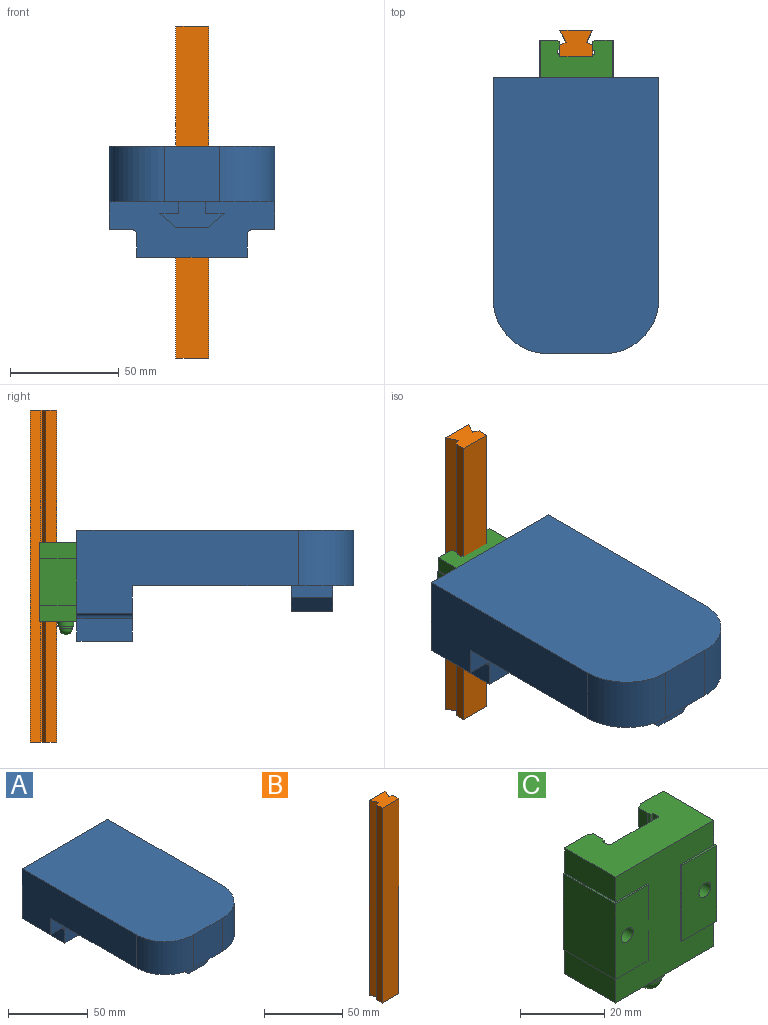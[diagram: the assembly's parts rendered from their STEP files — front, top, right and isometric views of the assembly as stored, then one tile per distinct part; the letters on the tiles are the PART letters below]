
ASSEMBLY  parts=3 mates=4
PART A: 25 faces, bbox 76.2x127x50.8 mm
  f0: plane 76.2x25.4mm, normal (0,-1,0), area 1615.7mm2, adj f1,f2,f3,f4,f5,f7,f8,f9
  f1: plane 50.8x25.4mm, normal (0,0,-1), area 1290.3mm2, adj f0,f2,f10,f11
  f2: plane 25.4x10.16mm, normal (1,0,0), area 258.1mm2, adj f0,f1,f3,f11
  f3: cylinder r=2.54mm len=25.4mm, axis (0,-1,0), area 101.3mm2, adj f0,f2,f4,f11
  f4: plane 25.4x10.16mm, normal (0,0,-1), area 258.1mm2, adj f0,f3,f5,f11
  f5: plane 101.6x38.1mm, normal (1,0,0), area 2903.2mm2, adj f0,f4,f6,f11,f13,f15
  f6: plane 127x76.2mm, normal (0,0,1), area 9400.5mm2, adj f5,f7,f11,f12,f14,f15
  f7: plane 101.6x38.1mm, normal (-1,0,0), area 2903.2mm2, adj f0,f6,f8,f11,f13,f14
  f8: plane 25.4x10.16mm, normal (0,0,-1), area 258.1mm2, adj f0,f7,f9,f11
  f9: cylinder r=2.54mm len=25.4mm, axis (0,-1,0), area 101.3mm2, adj f0,f8,f10,f11
  f10: plane 25.4x10.16mm, normal (-1,0,0), area 258.1mm2, adj f0,f1,f9,f11
  f11: plane 76.2x50.8mm, normal (0,1,0), area 3551.1mm2, adj f1,f2,f3,f4,f5,f6,f7,f8
  f12: plane 25.4x25.4mm, normal (0,-1,0), area 645.2mm2, adj f6,f13,f14,f15
  f13: plane 101.6x76.2mm, normal (0,0,-1), area 7223.1mm2, adj f0,f5,f7,f12,f14,f15,f16,f22
  f14: cylinder r=25.4mm len=25.4mm, axis (0,0,1), area 1013.4mm2, adj f6,f7,f12,f13
  f15: cylinder r=25.4mm len=25.4mm, axis (0,0,-1), area 1013.4mm2, adj f5,f6,f12,f13
  f16: plane 19.05x5.44mm, normal (-1,0,0), area 103.6mm2, adj f13,f17,f23,f24
  f17: plane 19.05x8.37mm, normal (0,0,1), area 159.4mm2, adj f16,f18,f23,f24
  f18: plane 19.05x7.1mm, normal (-0.67,0,-0.75), area 181.4mm2, adj f17,f19,f23,f24
  f19: plane 19.05x15.24mm, normal (0,0,-1), area 290.3mm2, adj f18,f20,f23,f24
  f20: plane 19.05x7.1mm, normal (0.67,0,-0.75), area 181.4mm2, adj f19,f21,f23,f24
  f21: plane 19.05x8.37mm, normal (0,0,1), area 159.4mm2, adj f20,f22,f23,f24
  f22: plane 19.05x5.44mm, normal (1,0,0), area 103.6mm2, adj f13,f21,f23,f24
  f23: plane 29.43x11.79mm, normal (0,-1,0), area 210.9mm2, adj f13,f16,f17,f18,f19,f20,f21,f22
  f24: plane 29.43x11.79mm, normal (0,1,0), area 210.9mm2, adj f13,f16,f17,f18,f19,f20,f21,f22
PART B: 12 faces, bbox 15x12x152.4 mm
  f0: plane 152.4x4.84mm, normal (0.89,-0.46,0), area 830.8mm2, adj f1,f9,f10,f11
  f1: plane 152.4x15mm, normal (0,1,0), area 2286.1mm2, adj f0,f2,f10,f11
  f2: plane 152.4x4.84mm, normal (-0.89,-0.46,0), area 830.8mm2, adj f1,f6,f10,f11
  f3: plane 152.4x5mm, normal (-1,0,0), area 762mm2, adj f4,f7,f10,f11
  f4: plane 152.4x15mm, normal (0,-1,0), area 2286.1mm2, adj f3,f5,f10,f11
  f5: plane 152.4x5mm, normal (1,0,0), area 762mm2, adj f4,f8,f10,f11
  f6: plane 152.4x0.66mm, normal (-0.88,-0.47,0), area 113.3mm2, adj f2,f7,f10,f11
  f7: plane 152.4x2.85mm, normal (-0.47,0.88,0), area 490.1mm2, adj f3,f6,f10,f11
  f8: plane 152.4x2.85mm, normal (0.47,0.88,0), area 490.1mm2, adj f5,f9,f10,f11
  f9: plane 152.4x0.66mm, normal (0.88,-0.47,0), area 113.3mm2, adj f0,f8,f10,f11
  f10: plane 15x12mm, normal (0,0,-1), area 160.1mm2, adj f0,f1,f2,f3,f4,f5,f6,f7
  f11: plane 15x12mm, normal (0,0,1), area 160.1mm2, adj f0,f1,f2,f3,f4,f5,f6,f7
PART C: 46 faces, bbox 34x17.5x42.5 mm
  f0: plane 11.25x0.5mm, normal (0,0,1), area 5.6mm2, adj f2,f10,f32,f37
  f1: plane 17.5x11.75mm, normal (0,0,-1), area 14.4mm2, adj f2,f4,f10,f11,f34,f37
  f2: plane 22x11.75mm, normal (0,-1,0), area 245.9mm2, adj f0,f1,f32,f33,f34,f37,f39
  f3: plane 17x7.25mm, normal (-1,0,0), area 123.2mm2, adj f8,f10,f19,f29
  f4: plane 17x7.25mm, normal (1,0,0), area 123.2mm2, adj f1,f9,f10,f11
  f5: plane 17x7.25mm, normal (1,0,0), area 123.2mm2, adj f8,f10,f11,f33
  f6: plane 36.5x0.8mm, normal (0.95,-0.3,0), area 30.7mm2, adj f8,f9,f18,f27
  f7: plane 36.5x1.5mm, normal (0.47,0.88,0), area 61.9mm2, adj f8,f9,f19,f27
  f8: plane 33x17mm, normal (0,0,1), area 454.8mm2, adj f3,f5,f6,f7,f10,f11,f12,f13
  f9: plane 33x17mm, normal (0,0,-1), area 410.7mm2, adj f4,f6,f7,f10,f11,f12,f13,f14
  f10: plane 36.5x33mm, normal (0,-1,0), area 720.5mm2, adj f0,f1,f3,f4,f5,f8,f9,f20
  f11: plane 36.5x8mm, normal (0,1,0), area 270.9mm2, adj f1,f4,f5,f8,f9,f12,f33,f34
  f12: plane 36.5x1.5mm, normal (-0.47,0.88,0), area 61.9mm2, adj f8,f9,f11,f28
  f13: plane 36.5x0.8mm, normal (-0.95,-0.3,0), area 30.7mm2, adj f8,f9,f14,f28
  f14: plane 36.5x0.61mm, normal (0,-1,0), area 22.1mm2, adj f8,f9,f13,f15
  f15: plane 36.5x1.62mm, normal (-1,0,0), area 59mm2, adj f8,f9,f14,f21
  f16: plane 36.5x15.71mm, normal (0,1,0), area 573.5mm2, adj f8,f9,f21,f22
  f17: plane 36.5x1.62mm, normal (1,0,0), area 59mm2, adj f8,f9,f18,f22
  f18: plane 36.5x0.61mm, normal (0,-1,0), area 22.1mm2, adj f6,f8,f9,f17
  f19: plane 36.5x8mm, normal (0,1,0), area 270.9mm2, adj f3,f7,f8,f9,f20,f29,f35,f36
  f20: plane 17.5x7.25mm, normal (-1,0,0), area 123.3mm2, adj f9,f10,f19,f30,f31,f35
  f21: cylinder r=0.5mm len=36.5mm, axis (0,0,1), area 28.7mm2, adj f8,f9,f15,f16
  f22: cylinder r=0.5mm len=36.5mm, axis (0,0,-1), area 28.7mm2, adj f8,f9,f16,f17
  f23: cylinder r=3.75mm len=7.5mm, axis (0,0,1), area 47.1mm2, adj f9,f24
  f24: plane 7.5x7.5mm, normal (0,0,-1), area 15.9mm2, adj f23,f25
  f25: cylinder r=3mm len=6mm, axis (0,0,1), area 18.8mm2, adj f24,f26
  f26: sphere r=3mm, area 56.5mm2, adj f25
  f27: plane 36.5x3.04mm, normal (1,0,0), area 111mm2, adj f6,f7,f8,f9
  f28: plane 36.5x3.04mm, normal (-1,0,0), area 111mm2, adj f8,f9,f12,f13
  f29: plane 17.5x11.25mm, normal (0,0,1), area 14.1mm2, adj f3,f10,f19,f31,f36,f38
  f30: plane 10.75x0.5mm, normal (0,0,-1), area 5.4mm2, adj f10,f20,f31,f38
  f31: plane 22x11.25mm, normal (0,-1,0), area 234.9mm2, adj f20,f29,f30,f35,f36,f38,f40
  f32: plane 0.5x0mm, normal (-1,0,0), area 0mm2, adj f0,f2,f10,f33
  f33: plane 17.5x0.5mm, normal (0,0,1), area 8.8mm2, adj f2,f5,f11,f32,f34
  f34: plane 22x17.5mm, normal (1,0,0), area 385mm2, adj f1,f2,f11,f33
  f35: plane 17.5x0.5mm, normal (0,0,-1), area 8.8mm2, adj f19,f20,f31,f36
  f36: plane 22x17.5mm, normal (-1,0,0), area 384.9mm2, adj f19,f29,f31,f35
  f37: plane 22x0.5mm, normal (-1,0,0), area 11mm2, adj f0,f1,f2,f10
  f38: plane 22x0.5mm, normal (1,0,0), area 11mm2, adj f10,f29,f30,f31
  f39: cylinder r=2mm len=10.5mm, axis (0,-1,0), area 131.9mm2, adj f2,f42
  f40: cylinder r=2mm len=10.5mm, axis (0,-1,0), area 131.9mm2, adj f31,f41,f44
  f41: plane 1.86x1.38mm, normal (0,-1,0), area 0mm2, adj f40,f45
  f42: plane 4.2x4.2mm, normal (0,1,0), area 1.3mm2, adj f39,f43
  f43: cylinder r=2.1mm len=7mm, axis (0,-1,0), area 92.4mm2, adj f11,f42
  f44: plane 4.2x4.2mm, normal (0,1,0), area 1.3mm2, adj f40,f45
  f45: cylinder r=2.1mm len=7mm, axis (0,-1,0), area 92.4mm2, adj f19,f41,f44
PLACE A t=(-30.83,7.73,49.15)mm
PLACE B t=(-23.25,54.53,-22.59)mm fixed
PLACE C t=(-14.25,33.13,32.62)mm
MATE slider B.f10 <-> C.f9  axis (0,0,-1) through (-30.75,48.3,-22.59)mm
MATE fastened C.f10 <-> A.f11  axis (0,-1,0) through (-30.83,33.13,50.87)mm
MATE planar A.f6 <-> C.f8  axis (0,0,1) through (-30.83,-28.66,74.55)mm
MATE parallel C.f16 <-> B.f4  axis (0,1,0) through (-30.75,43.38,32.62)mm
